# Revit family: Door_Swing_Syntegra-Integrated_DoorSysInc_Single-90-Stair Lever-Lever
name_source: partatom
category: Doors
revit_build: Autodesk Revit 2016 (Build: 20150714_1515(x64)
units: mm (PartAtom-declared; Revit-internal decimal feet)

## family parameters
Always vertical = Yes
Cut with Voids When Loaded = No
Host = Wall
OmniClass Number = 23.30.10.17.24
OmniClass Title = Balanced Doors
Room Calculation Point = No
Shared = No

## types (8) — shared parameters
Analytic Construction = <None>
Assembly Code = B2030
Construction Details = http://www.arcat.com
Description = Door Systems Inc Syntegra Single Door System - Single 90 No Pocket as Specified
Door Frame Finish = Metal - White
Door Slab Finish = Metal - RAL 7048 - Pearl Mouse Grey
Fire Rating = as Specified
Function = Interior
Height = 0' - 0"
Jamb Thickness_Sides = 0' - 2"
Jamb Thickness_Top = 0' - 2"
Keynote = 08 17 00
Manufacturer = Door Systems, Inc
Manufacturer Website = http://www.doorsysinc.com
Model = Single 90 No Pocket
Product Data = http://www.arcat.com
RO Spacing Sides = 0' - 0 1/2"
RO Spacing Top = 0' - 0 1/2"
Sales Information = http://www.doorsysinc.com
Specification = http://www.arcat.com
Thickness = 0' - 0"
URL = http://www.doorsysinc.com
Wall Closure = By host
Width = 0' - 0"
zero-valued in all types: Expected Lifespan (Years), Maintenance Schedule (Months), R-Value, Warranty Duration (Years)

## type names (no varying parameters)
- Stairwell
- Special Application
- High Use or Abuse
- Hospital
- Elevator Lobby Protection
- Elevator Shaft Protection
- Cross Corridor
- Area Separation

## geometry (parser evidence)
native form markers: Sweep x21
no freeform markers — native parametric forms only
